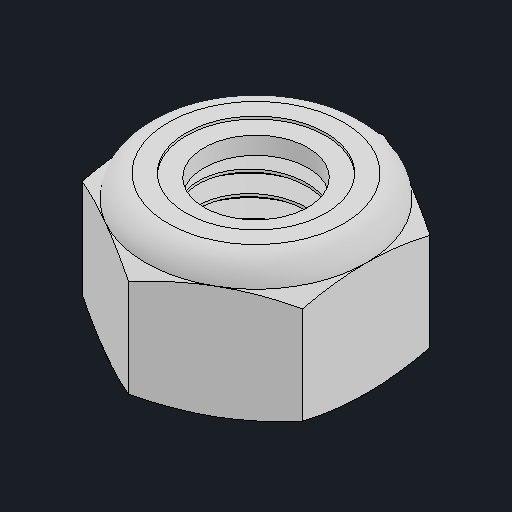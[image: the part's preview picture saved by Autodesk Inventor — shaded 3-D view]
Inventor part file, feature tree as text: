
AUTODESK INVENTOR PART (.ipt)
format: ipt  version: 2024.2 (Build 282272000, 272)  size: 314,880 bytes
history: native  units: mm
features: other x3, revolve x1
ambient origin geometry x8: Origin, YZ Plane, XZ Plane, XY Plane, X Axis, Y Axis, Z Axis, Center Point
bodies: Body1 (feature_tree), Body2 (feature_tree)
feature tree (4):
  other  "솔리드1"
  other  "솔리드2"
  other  "Cut-Revolve4"
  revolve  "Revolve2"  [1 undecoded]
note: 1 required parameter value undecoded (feature->parameter linkage not recoverable at this tier; creation-order binding heuristic only, values carry confidence <= 0.55)
